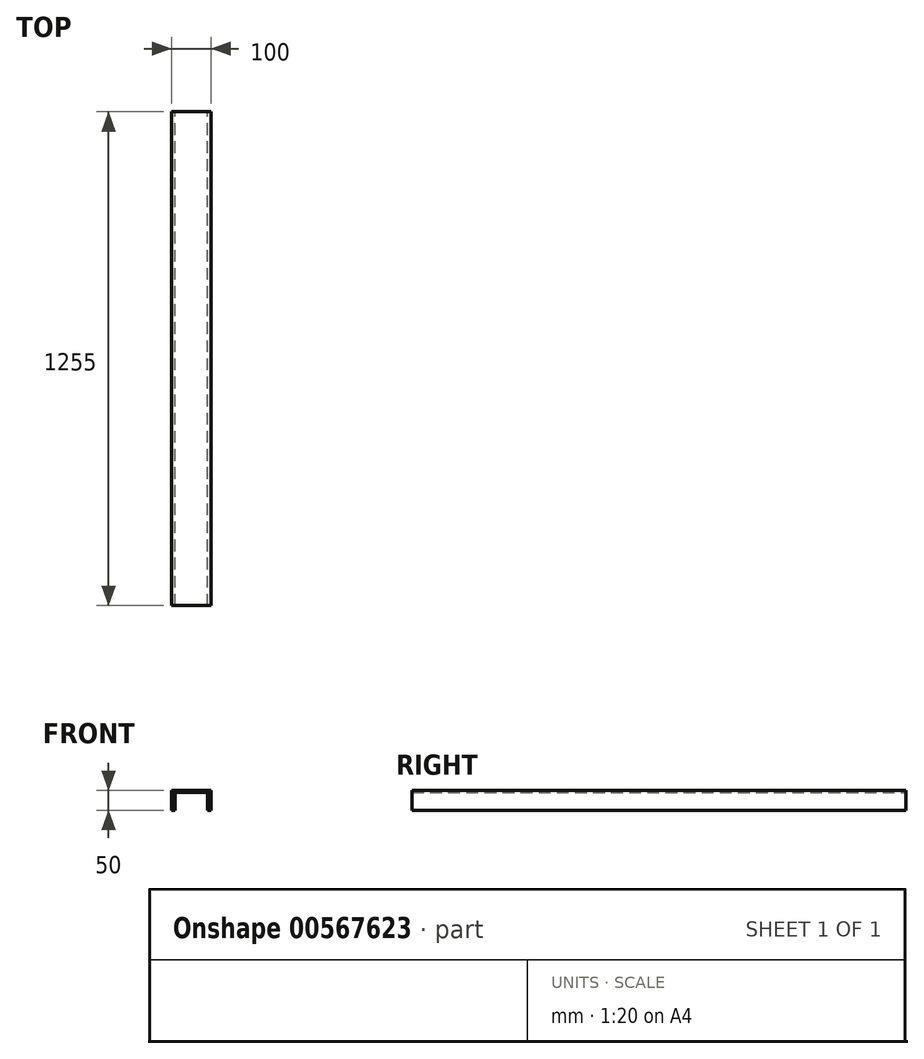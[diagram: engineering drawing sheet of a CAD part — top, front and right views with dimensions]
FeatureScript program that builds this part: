
annotation { "Feature Type Name" : "Feature", "Feature Type Description" : "" }
export const myFeature = defineFeature(function(context is Context, id is Id, definition is map)
    precondition{}
    {
        {
            var Q0;
            Q0=qCreatedBy(makeId("Front.planeOp"),FACE);
            var sketch = newSketch(context, id + "F0", { "sketchPlane" : qUnion([Q0])});
            skLineSegment(sketch, "E0", {"start": v(-47.76, 39.74) * mm, "end": v(52.24, 39.74) * mm});
            skLineSegment(sketch, "E1", {"start": v(-47.76, 39.74) * mm, "end": v(-47.76, -10.26) * mm});
            skLineSegment(sketch, "E2", {"start": v(52.24, 39.74) * mm, "end": v(52.24, -10.26) * mm});
            skLineSegment(sketch, "E3", {"start": v(52.24, -10.26) * mm, "end": v(43.74, -10.26) * mm});
            skLineSegment(sketch, "E4", {"start": v(43.74, -10.26) * mm, "end": v(43.74, 34.74) * mm});
            skLineSegment(sketch, "E5", {"start": v(43.74, 34.74) * mm, "end": v(-39.26, 34.74) * mm});
            skLineSegment(sketch, "E6", {"start": v(-39.26, 34.74) * mm, "end": v(-39.26, -10.26) * mm});
            skLineSegment(sketch, "E7", {"start": v(-39.26, -10.26) * mm, "end": v(-47.76, -10.26) * mm});
            skSolve(sketch);
        }
        {
            var Q0;
            Q0 = qSketchRegion(id + "F0", true);
            extrude(context, id + "F1", {"entities" : qUnion([Q0]), "depth" : 1255 * mm, "offsetDistance" : 25 * mm});
        }
    });
